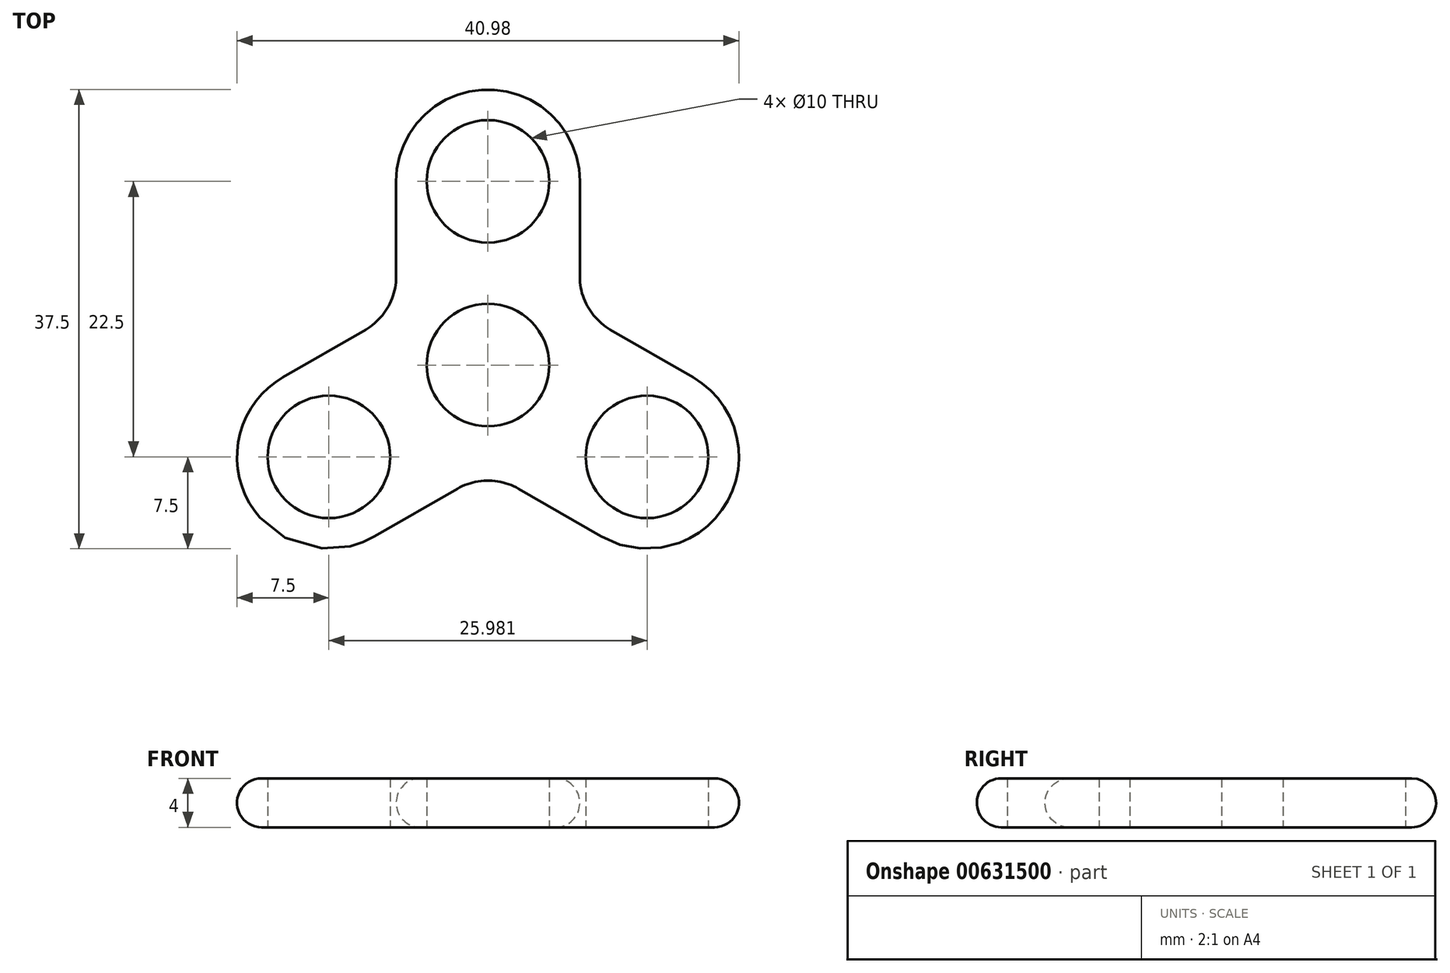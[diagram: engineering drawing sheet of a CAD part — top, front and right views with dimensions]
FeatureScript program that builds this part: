
annotation { "Feature Type Name" : "Feature", "Feature Type Description" : "" }
export const myFeature = defineFeature(function(context is Context, id is Id, definition is map)
    precondition{}
    {
        {
            var Q0;
            Q0=qCreatedBy(makeId("Top.planeOp"),FACE);
            var sketch = newSketch(context, id + "F0", { "sketchPlane" : qUnion([Q0])});
            skCircle(sketch, "E0", {"center": v(0, 0) * mm, "radius": 5 * mm});
            skCircle(sketch, "E1", {"center": v(0, 0) * mm, "radius": 7.5 * mm});
            skLineSegment(sketch, "E2", {"start": v(0, 0) * mm, "end": v(0, 7.5) * mm, "construction": true});
            skLineSegment(sketch, "E3", {"start": v(0, 7.5) * mm, "end": v(0, 15) * mm, "construction": true});
            skCircle(sketch, "E4", {"center": v(0, 15) * mm, "radius": 7.5 * mm});
            skCircle(sketch, "E5", {"center": v(0, 15) * mm, "radius": 5 * mm});
            skCircle(sketch, "E6.1.0", {"center": v(-13, -7.5) * mm, "radius": 7.5 * mm});
            skCircle(sketch, "E6.1.1", {"center": v(-13, -7.5) * mm, "radius": 5 * mm});
            skCircle(sketch, "E6.2.0", {"center": v(13, -7.5) * mm, "radius": 7.5 * mm});
            skCircle(sketch, "E6.2.1", {"center": v(13, -7.5) * mm, "radius": 5 * mm});
            skLineSegment(sketch, "E7", {"start": v(0, 15) * mm, "end": v(7.5, 15) * mm, "construction": true});
            skLineSegment(sketch, "E8", {"start": v(7.5, 15) * mm, "end": v(7.5, 0) * mm});
            skLineSegment(sketch, "E9.MirrorCS", {"start": v(-7.5, 15) * mm, "end": v(-7.5, 0) * mm});
            skLineSegment(sketch, "E10.1.0", {"start": v(-16.74, -1) * mm, "end": v(-3.75, 6.5) * mm});
            skLineSegment(sketch, "E10.1.1", {"start": v(-9.24, -14) * mm, "end": v(3.75, -6.5) * mm});
            skLineSegment(sketch, "E10.2.0", {"start": v(9.24, -14) * mm, "end": v(-3.75, -6.5) * mm});
            skLineSegment(sketch, "E10.2.1", {"start": v(16.74, -1) * mm, "end": v(3.75, 6.5) * mm});
            skSolve(sketch);
        }
        {
            var Q0;
            Q0 = qSketchRegion(id + "F0", true);
            var Q1;
            Q1=makeQuery(id+"F0.imprint","IMPRINT",FACE,{"disambiguationData":[TD([[makeQuery(id+"F0.imprint","IMPRINT",EDGE,{"derivedFrom":sQuery(id+"F0.wireOp",EDGE,"E0")}),-1.0]])]});
            extrude(context, id + "F1", {"entities" : qUnion([Q0, Q1]), "depth" : 4 * mm, "offsetDistance" : 25 * mm});
        }
        {
            var Q0;
            Q0=makeQuery(id+"F1.opExtrude","SWEPT_EDGE",EDGE,{"disambiguationData":[OSD([sQuery(id+"F0.wireOp",EDGE,"E10.1.1"),sQuery(id+"F0.wireOp",EDGE,"E10.2.0")])]});
            var Q1;
            Q1=makeQuery(id+"F1.opExtrude","SWEPT_EDGE",EDGE,{"disambiguationData":[OSD([sQuery(id+"F0.wireOp",EDGE,"E8"),sQuery(id+"F0.wireOp",EDGE,"E10.2.1")])]});
            var Q2;
            Q2=makeQuery(id+"F1.opExtrude","SWEPT_EDGE",EDGE,{"disambiguationData":[OSD([sQuery(id+"F0.wireOp",EDGE,"E9.MirrorCS"),sQuery(id+"F0.wireOp",EDGE,"E10.1.0")])]});
            fillet(context, id + "F2", {"entities" : qUnion([Q0, Q1, Q2]), "radius" : 5 * mm, "tangentPropagation" : true, "allowEdgeOverflow" : false});
        }
        {
            var Q0;
            Q0=makeQuery(id+"F1.opExtrude","CAP_EDGE",EDGE,{"disambiguationData":[OSD([sQuery(id+"F0.wireOp",EDGE,"E10.1.0")])],"isStart":true});
            var Q1;
            Q1=makeQuery(id+"F1.opExtrude","CAP_EDGE",EDGE,{"disambiguationData":[OSD([sQuery(id+"F0.wireOp",EDGE,"E10.1.0")])],"isStart":false});
            fillet(context, id + "F3", {"entities" : qUnion([Q0, Q1]), "radius" : 2 * mm, "tangentPropagation" : true, "allowEdgeOverflow" : false});
        }
    });
